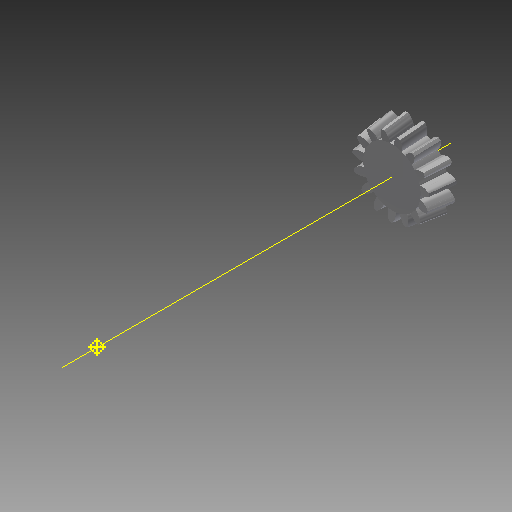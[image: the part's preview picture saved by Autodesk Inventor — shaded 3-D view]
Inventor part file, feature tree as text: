
AUTODESK INVENTOR PART (.ipt)
format: ipt  version: 2017 (Build 210142000, 142)  size: 500,736 bytes
history: native  units: mm
features: other x24, loft x2, pattern_circular x2, sketch x1
ambient origin geometry x6: Origin, XZ Plane, X Axis, Y Axis, Z Axis, Center Point
bodies: Solid1 (feature_tree)
feature tree (29):
  other  "Top Point"
  other  "Mesh Plane2"
  other  "Teeth Body"
  other  "Start Point"
  other  "Tooth Plane"
  other  "Start Sketch"
  other  "End Point"
  other  "3D Sketch Right"
  other  "End Plane Right"
  loft  "Loft Right"
  pattern_circular  "Circular Pattern Right"  [2 undecoded]
  other  "3D Sketch Left"
  other  "End Plane Left"
  loft  "Loft Left"
  pattern_circular  "Circular Pattern Left"  [2 undecoded]
  other  "Fix Body"
  other  "Mesh Plane"
  other  "Top Plane"
  other  "Teeth Body Sketch"
  other  "End Plane"
  other  "End Sketch"
  other  "Helical Curve Left"
  other  "End Sketch Left"
  other  "Body Sketch"
  sketch  "Sketch6"  dims[d0=38.1mm d1=32.044179mm d2=42.954701mm d3=12.7mm d4=164.819921mm d5=90.0deg d7=7.248858mm d8=8.457324mm d9=15.796036mm d11=12.974573mm d12=6.690202mm d15=7.805534mm d16=14.578664mm d17=0.0mm d18=90.0deg d19=0.0mm d20=90.0deg d21=150.0mm d22=360.0deg d26=314.208686mm d27=12.889057mm d28=38.1mm d29=-1.148766mm d30=6.690202mm d31=7.805534mm d32=14.578664mm d35=0.0mm d37=0.0mm d39=0.0mm d40=90.0deg d41=150.0mm d42=360.0deg d46=90.0deg d47=90.0deg d48=0.0mm d49=0.0mm d50=90.0deg d51=2.094395mm d52=0.0mm d53=0.0mm d54=0.0mm d56=19.705453mm d57=23.267285mm d58=15.469418mm d59=21.474118mm d60=14.277218mm d61=21.474118mm d62=14.277218mm d63=90.0deg d64=90.0deg d65=314.208686mm d66=31.5mm d67=38.1mm d68=-1.148766mm d69=12.889057mm d70=7.805534mm d71=14.578664mm d72=6.690202mm d73=14.277218mm d74=21.474118mm d75=0.0mm d76=90.0deg d77=0.0mm d78=90.0deg d79=0.0mm d80=90.0deg d81=150.0mm d82=360.0deg d84=10.0mm d85=20.0mm d86=20.0mm d87=10.0mm d88=0.0mm d89=0.0mm]
  other  "Srf1"
  other  "Helical Curve Right"
  other  "End Sketch Right"
  other  "Pitch Diameter"
note: 4 required parameter values undecoded (feature->parameter linkage not recoverable at this tier; creation-order binding heuristic only, values carry confidence <= 0.55)
